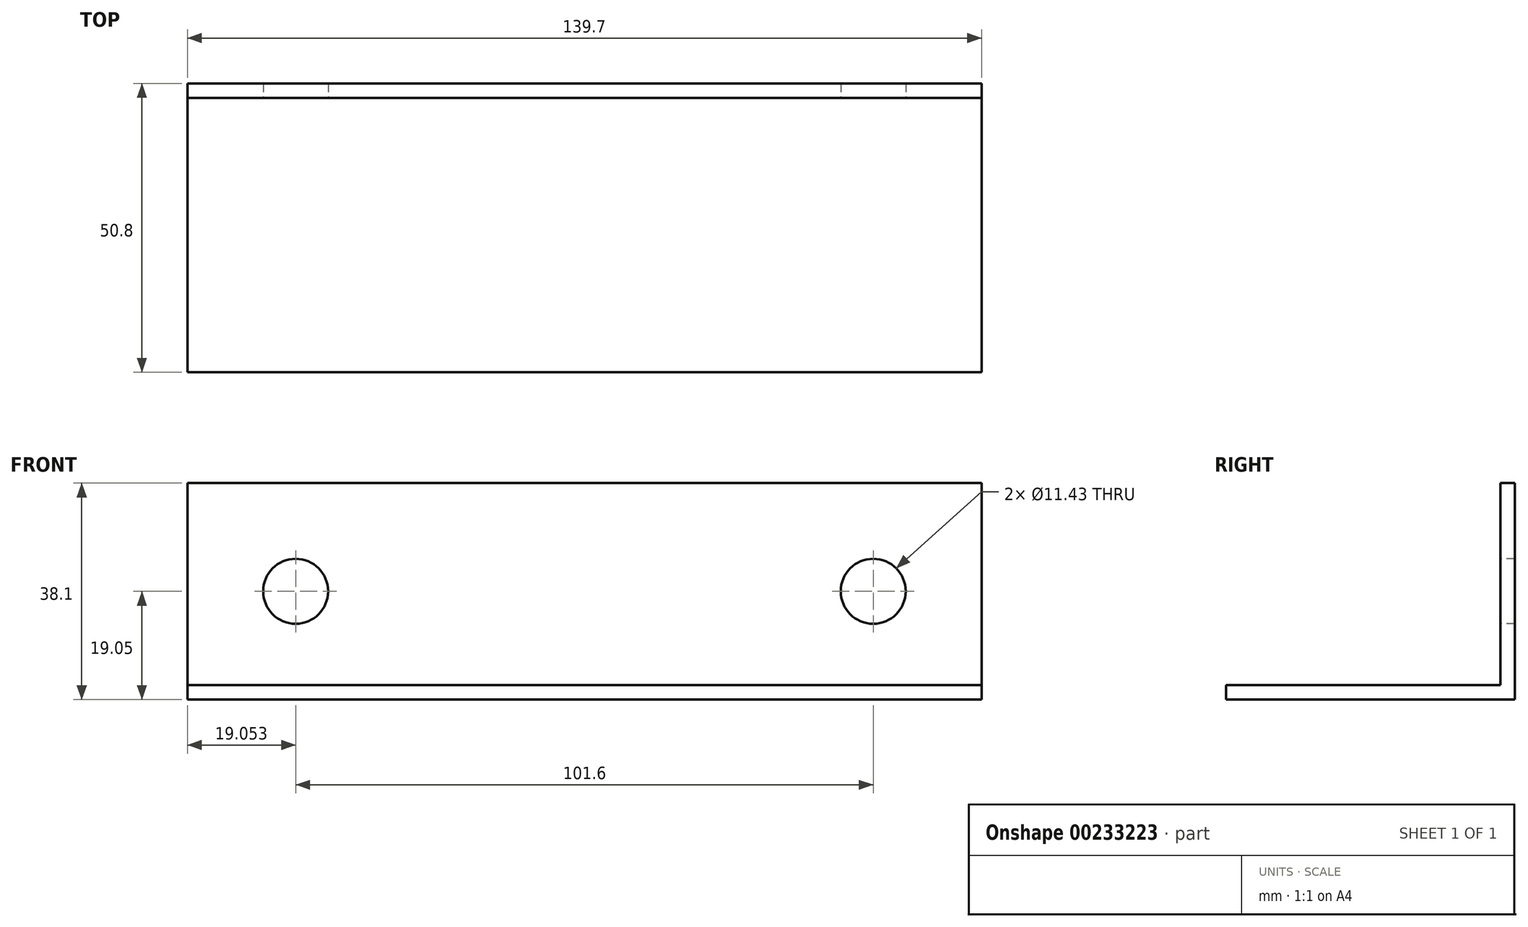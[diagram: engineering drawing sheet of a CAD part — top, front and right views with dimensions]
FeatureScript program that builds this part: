
annotation { "Feature Type Name" : "Feature", "Feature Type Description" : "" }
export const myFeature = defineFeature(function(context is Context, id is Id, definition is map)
    precondition{}
    {
        {
            var Q0;
            Q0=qCreatedBy(makeId("Front.planeOp"),FACE);
            var sketch = newSketch(context, id + "F0", { "sketchPlane" : qUnion([Q0])});
            skLineSegment(sketch, "E0.bottom", {"start": v(-69.14, 0) * mm, "end": v(70.56, 0) * mm});
            skLineSegment(sketch, "E0.top", {"start": v(-69.14, -38.1) * mm, "end": v(70.56, -38.1) * mm});
            skLineSegment(sketch, "E0.left", {"start": v(-69.14, 0) * mm, "end": v(-69.14, -38.1) * mm});
            skLineSegment(sketch, "E0.right", {"start": v(70.56, 0) * mm, "end": v(70.56, -38.1) * mm});
            skCircle(sketch, "E1", {"center": v(-50.09, -19.05) * mm, "radius": 3.18 * mm});
            skCircle(sketch, "E2", {"center": v(51.51, -19.05) * mm, "radius": 3.18 * mm});
            skSolve(sketch);
        }
        {
            var Q0;
            Q0 = qSketchRegion(id + "F0", true);
            extrude(context, id + "F1", {"entities" : qUnion([Q0]), "depth" : 50.8 * mm});
        }
        {
            var Q0;
            Q0=makeQuery(id+"F1.opExtrude","SWEPT_FACE",FACE,{"disambiguationData":[OSD([sQuery(id+"F0.wireOp",EDGE,"E0.bottom")])]});
            var Q1;
            Q1=makeQuery(id+"F1.opExtrude","CAP_FACE",FACE,{"disambiguationData":[OSD([sQuery(id+"F0.wireOp",EDGE,"E0.bottom"),sQuery(id+"F0.wireOp",EDGE,"E0.top"),sQuery(id+"F0.wireOp",EDGE,"E0.left"),sQuery(id+"F0.wireOp",EDGE,"E0.right")])],"isStart":false});
            var Q2;
            Q2=makeQuery(id+"F1.opExtrude","SWEPT_FACE",FACE,{"disambiguationData":[OSD([sQuery(id+"F0.wireOp",EDGE,"E0.right")])]});
            var Q3;
            Q3=makeQuery(id+"F1.opExtrude","SWEPT_FACE",FACE,{"disambiguationData":[OSD([sQuery(id+"F0.wireOp",EDGE,"E0.left")])]});
            shell(context, id + "F2", {"entities" : qUnion([Q0, Q1, Q2, Q3]), "thickness" : 2.54 * mm});
        }
        {
            var Q0;
            {var subQ0=sQuery(id+"F0.wireOp",EDGE,"E1");var subQ1=sQuery(id+"F0.wireOp",EDGE,"E0.right");var subQ2=sQuery(id+"F0.wireOp",EDGE,"E0.left");var subQ3=sQuery(id+"F0.wireOp",EDGE,"E0.top");var subQ4=sQuery(id+"F0.wireOp",EDGE,"E0.bottom");Q0=makeQuery(id+"F2.opShell","OFFSET_FACE",FACE,{"disambiguationData":[OSD([subQ4,subQ3,subQ2,subQ1,subQ0]),TDD([makeQuery(id+"F1.opExtrude","CAP_FACE",FACE,{"disambiguationData":[OSD([subQ4,subQ3,subQ2,subQ1,subQ0])],"isStart":false})])]});}
            extrude(context, id + "F3", {"entities" : qUnion([Q0]), "operationType" : NewBodyOperationType.REMOVE, "oppositeDirection" : true, "depth" : 62.48 * mm});
        }
    });
